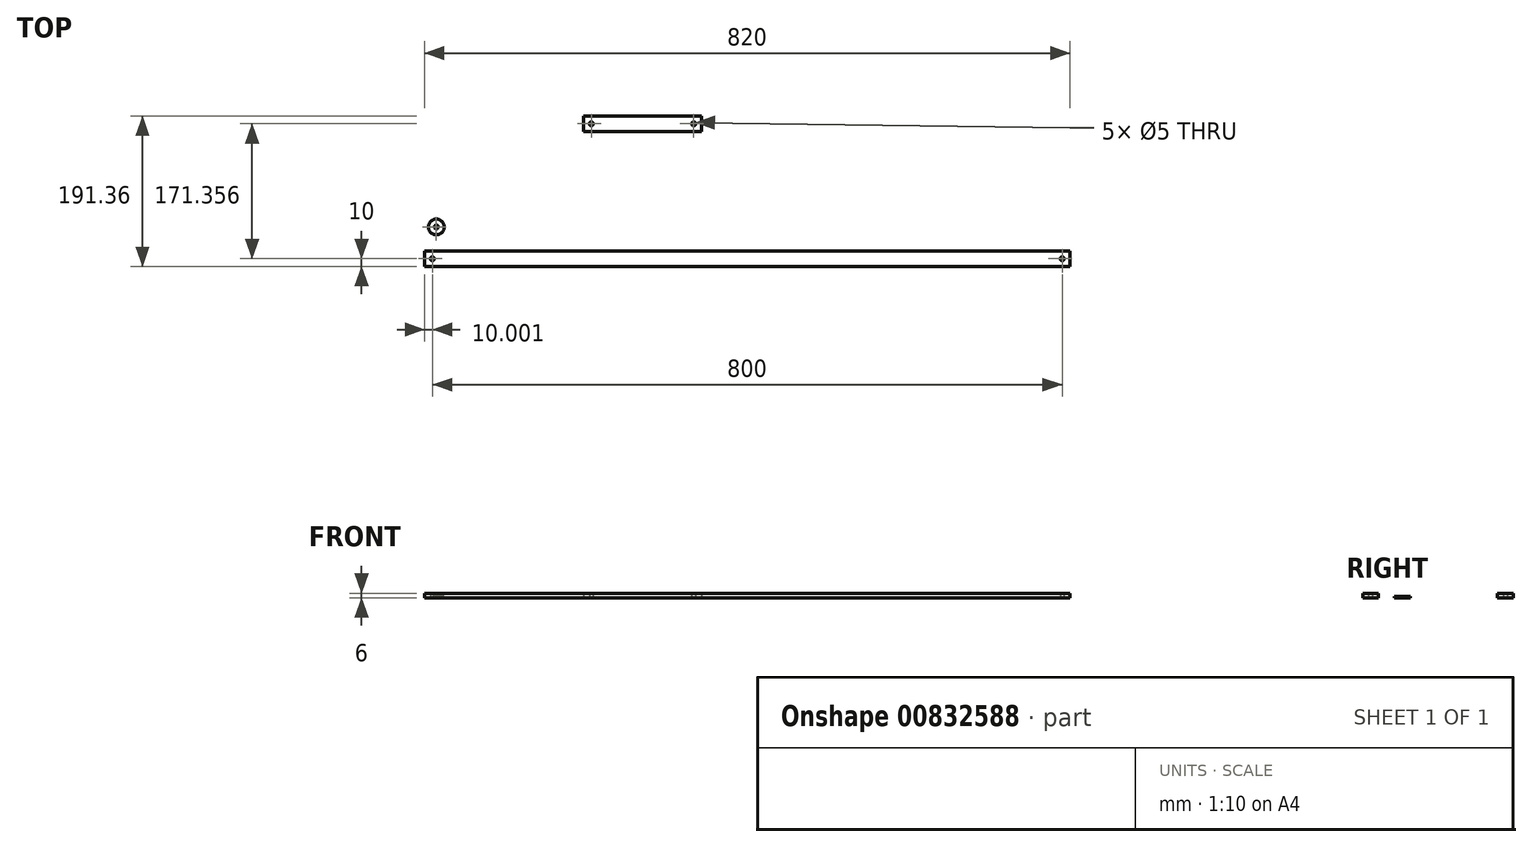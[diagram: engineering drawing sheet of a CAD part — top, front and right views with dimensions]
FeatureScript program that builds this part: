
annotation { "Feature Type Name" : "Feature", "Feature Type Description" : "" }
export const myFeature = defineFeature(function(context is Context, id is Id, definition is map)
    precondition{}
    {
        {
            var Q0;
            Q0=qCreatedBy(makeId("Top.planeOp"),FACE);
            var sketch = newSketch(context, id + "F0", { "sketchPlane" : qUnion([Q0])});
            skCircle(sketch, "E0", {"center": v(-187.8, 0) * mm, "radius": 2.5 * mm});
            skCircle(sketch, "E1", {"center": v(612.2, 0) * mm, "radius": 2.5 * mm});
            skLineSegment(sketch, "E2", {"start": v(622.2, 0) * mm, "end": v(622.2, 10) * mm});
            skLineSegment(sketch, "E3", {"start": v(-197.8, 0) * mm, "end": v(-197.8, 10) * mm});
            skLineSegment(sketch, "E4", {"start": v(-197.8, 10) * mm, "end": v(622.2, 10) * mm});
            skLineSegment(sketch, "E5", {"start": v(-197.8, 0) * mm, "end": v(-197.8, -10) * mm});
            skLineSegment(sketch, "E6", {"start": v(-197.8, -10) * mm, "end": v(622.2, -10) * mm});
            skLineSegment(sketch, "E7", {"start": v(622.2, -10) * mm, "end": v(622.2, 0) * mm});
            skSolve(sketch);
        }
        {
            var Q0;
            Q0=makeQuery(id+"F0.imprint","IMPRINT",FACE,{"disambiguationData":[TD([[makeQuery(id+"F0.imprint","IMPRINT",EDGE,{"derivedFrom":sQuery(id+"F0.wireOp",EDGE,"E0")}),-1.0]])]});
            extrude(context, id + "F1", {"entities" : qUnion([Q0]), "depth" : 6 * mm, "offsetDistance" : 25 * mm});
        }
        {
            var Q0;
            Q0=qCreatedBy(makeId("Top.planeOp"),FACE);
            var sketch = newSketch(context, id + "F2", { "sketchPlane" : qUnion([Q0])});
            skCircle(sketch, "E8", {"center": v(-182.85, 40.32) * mm, "radius": 10 * mm});
            skCircle(sketch, "E9", {"center": v(-182.85, 40.32) * mm, "radius": 2.5 * mm});
            skSolve(sketch);
        }
        {
            var Q0;
            Q0=makeQuery(id+"F2.imprint","IMPRINT",FACE,{"disambiguationData":[TD([[makeQuery(id+"F2.imprint","IMPRINT",EDGE,{"derivedFrom":sQuery(id+"F2.wireOp",EDGE,"E8")}),1.0]])]});
            extrude(context, id + "F3", {"entities" : qUnion([Q0]), "depth" : 2 * mm, "offsetDistance" : 25 * mm});
        }
        {
            var Q0;
            Q0=qCreatedBy(makeId("Top.planeOp"),FACE);
            var sketch = newSketch(context, id + "F4", { "sketchPlane" : qUnion([Q0])});
            skLineSegment(sketch, "E10.bottom", {"start": v(4.02, 181.36) * mm, "end": v(154.02, 181.36) * mm});
            skLineSegment(sketch, "E10.top", {"start": v(4.02, 161.36) * mm, "end": v(154.02, 161.36) * mm});
            skLineSegment(sketch, "E10.left", {"start": v(4.02, 181.36) * mm, "end": v(4.02, 161.36) * mm});
            skLineSegment(sketch, "E10.right", {"start": v(154.02, 181.36) * mm, "end": v(154.02, 161.36) * mm});
            skCircle(sketch, "E11", {"center": v(14.02, 171.36) * mm, "radius": 2.5 * mm});
            skCircle(sketch, "E12", {"center": v(144.02, 171.36) * mm, "radius": 2.5 * mm});
            skSolve(sketch);
        }
        {
            var Q0;
            Q0=makeQuery(id+"F4.imprint","IMPRINT",FACE,{"disambiguationData":[TD([[makeQuery(id+"F4.imprint","IMPRINT",EDGE,{"derivedFrom":sQuery(id+"F4.wireOp",EDGE,"E10.bottom")}),-1.0]])]});
            extrude(context, id + "F5", {"entities" : qUnion([Q0]), "depth" : 6 * mm, "offsetDistance" : 25 * mm});
        }
    });
